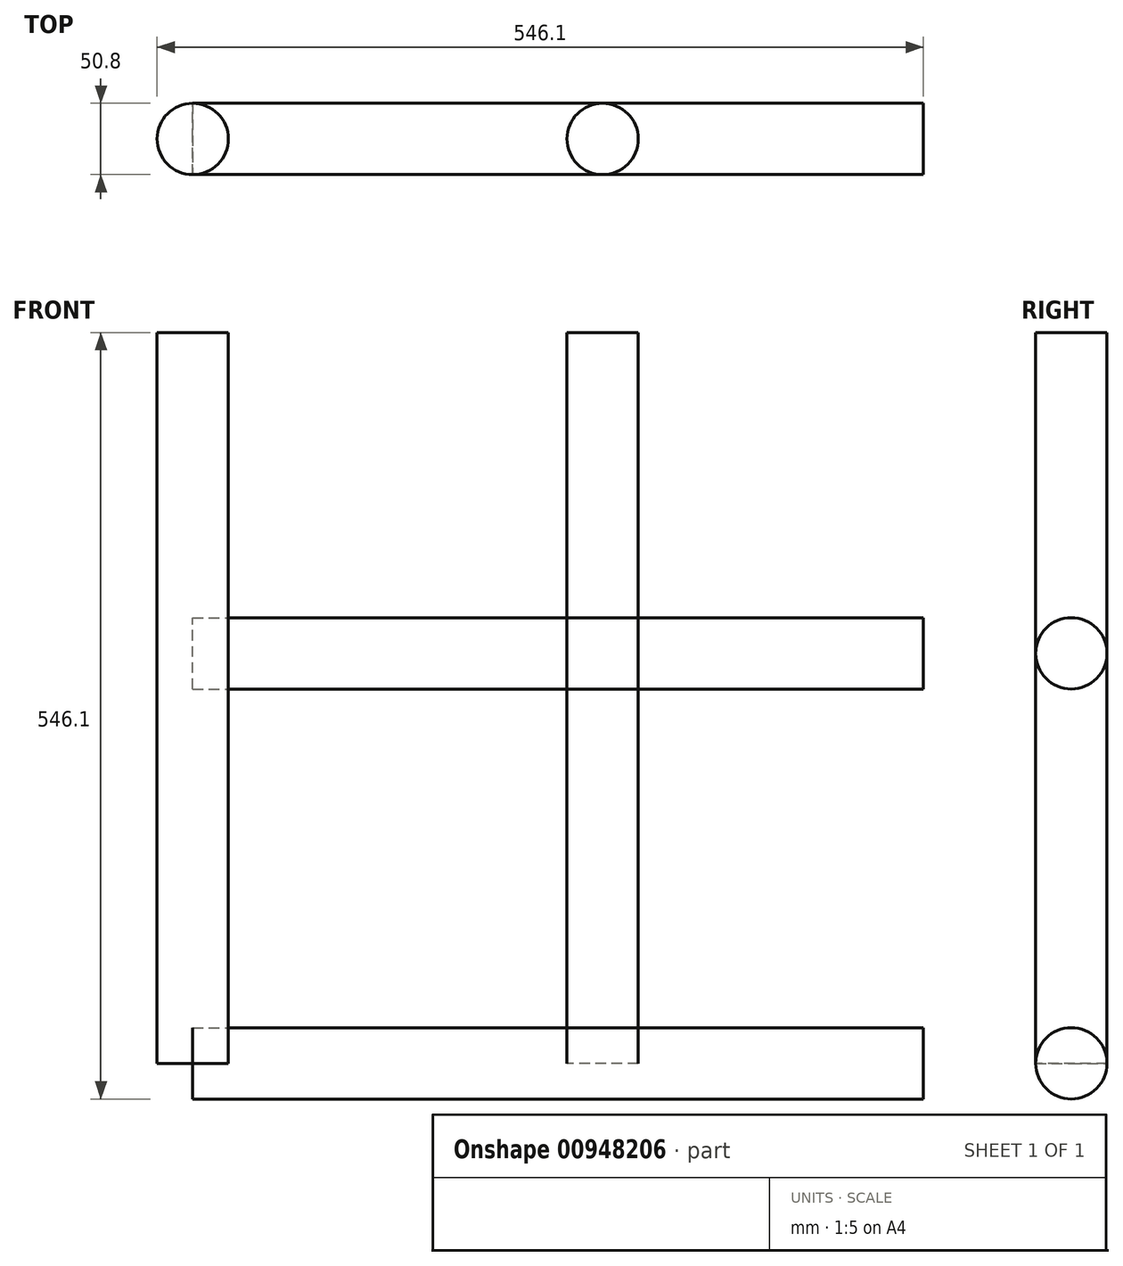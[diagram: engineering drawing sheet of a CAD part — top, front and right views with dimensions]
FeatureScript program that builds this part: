
annotation { "Feature Type Name" : "Feature", "Feature Type Description" : "" }
export const myFeature = defineFeature(function(context is Context, id is Id, definition is map)
    precondition{}
    {
        {
            var Q0;
            Q0=qCreatedBy(makeId("Right.planeOp"),FACE);
            cPlane(context, id + "F0", {"entities" : qUnion([Q0]), "cplaneType" : CPlaneType.OFFSET, "offset" : 292.1 * mm, "width" : 152.4 * mm, "height" : 152.4 * mm});
        }
        {
            var Q0;
            Q0=qCreatedBy(makeId("Top.planeOp"),FACE);
            cPlane(context, id + "F1", {"entities" : qUnion([Q0]), "cplaneType" : CPlaneType.OFFSET, "offset" : 292.1 * mm, "width" : 152.4 * mm, "height" : 152.4 * mm});
        }
        {
            var Q0;
            Q0=qCreatedBy(id+"F1.planeOp",FACE);
            var sketch = newSketch(context, id + "F2", { "sketchPlane" : qUnion([Q0])});
            skPoint(sketch, "E0.0", {"position": v(0, 0) * mm});
            skSolve(sketch);
        }
        {
            var Q0;
            Q0=qCreatedBy(id+"F0.planeOp",FACE);
            var sketch = newSketch(context, id + "F3", { "sketchPlane" : qUnion([Q0])});
            skPoint(sketch, "E1.0", {"position": v(0, 0) * mm});
            skPoint(sketch, "E2.0", {"position": v(0, 292.1) * mm});
            skSolve(sketch);
        }
        {
            var Q0;
            Q0=qCreatedBy(id+"F0.planeOp",FACE);
            cPlane(context, id + "F4", {"entities" : qUnion([Q0]), "cplaneType" : CPlaneType.OFFSET, "offset" : 228.6 * mm, "width" : 152.4 * mm, "height" : 152.4 * mm});
        }
        {
            var Q0;
            Q0=qCreatedBy(id+"F1.planeOp",FACE);
            cPlane(context, id + "F5", {"entities" : qUnion([Q0]), "cplaneType" : CPlaneType.OFFSET, "offset" : 228.6 * mm, "width" : 152.4 * mm, "height" : 152.4 * mm});
        }
        {
            var Q0;
            Q0=qCreatedBy(id+"F5.planeOp",FACE);
            var sketch = newSketch(context, id + "F6", { "sketchPlane" : qUnion([Q0])});
            skPoint(sketch, "E3.0", {"position": v(0, 0) * mm});
            skPoint(sketch, "E4.0", {"position": v(292.1, 0) * mm});
            skCircle(sketch, "E5", {"center": v(0, 0) * mm, "radius": 25.4 * mm});
            skCircle(sketch, "E6", {"center": v(292.1, 0) * mm, "radius": 25.4 * mm});
            skSolve(sketch);
        }
        {
            var Q0;
            Q0=qCreatedBy(id+"F4.planeOp",FACE);
            var sketch = newSketch(context, id + "F7", { "sketchPlane" : qUnion([Q0])});
            skPoint(sketch, "E7.0", {"position": v(0, 0) * mm});
            skPoint(sketch, "E8.0", {"position": v(0, 292.1) * mm});
            skCircle(sketch, "E9", {"center": v(0, 0) * mm, "radius": 25.4 * mm});
            skCircle(sketch, "E10", {"center": v(0, 292.1) * mm, "radius": 25.4 * mm});
            skSolve(sketch);
        }
        {
            var Q0;
            Q0=makeQuery(id+"F7.imprint","IMPRINT",FACE,{"disambiguationData":[TD([[makeQuery(id+"F7.imprint","IMPRINT",EDGE,{"derivedFrom":sQuery(id+"F7.wireOp",EDGE,"E9")}),1.0]])]});
            var Q1;
            Q1=makeQuery(id+"F7.imprint","IMPRINT",FACE,{"disambiguationData":[TD([[makeQuery(id+"F7.imprint","IMPRINT",EDGE,{"derivedFrom":sQuery(id+"F7.wireOp",EDGE,"E10")}),1.0]])]});
            var Q2;
            Q2=qCreatedBy(makeId("Right.planeOp"),FACE);
            extrude(context, id + "F8", {"entities" : qUnion([Q0, Q1]), "endBound" : BoundingType.UP_TO_SURFACE, "oppositeDirection" : true, "depth" : 25.4 * mm, "endBoundEntityFace" : qUnion([Q2]), "offsetDistance" : 25.4 * mm});
        }
        {
            var Q0;
            Q0=makeQuery(id+"F6.imprint","IMPRINT",FACE,{"disambiguationData":[TD([[makeQuery(id+"F6.imprint","IMPRINT",EDGE,{"derivedFrom":sQuery(id+"F6.wireOp",EDGE,"E5")}),1.0]])]});
            var Q1;
            Q1=makeQuery(id+"F6.imprint","IMPRINT",FACE,{"disambiguationData":[TD([[makeQuery(id+"F6.imprint","IMPRINT",EDGE,{"derivedFrom":sQuery(id+"F6.wireOp",EDGE,"E6")}),1.0]])]});
            var Q2;
            Q2=qCreatedBy(makeId("Top.planeOp"),FACE);
            extrude(context, id + "F9", {"entities" : qUnion([Q0, Q1]), "endBound" : BoundingType.UP_TO_SURFACE, "oppositeDirection" : true, "depth" : 25.4 * mm, "endBoundEntityFace" : qUnion([Q2]), "offsetDistance" : 25.4 * mm});
        }
    });
